# Revit family: P500236-030
name_source: partatom
category: Lighting Fixtures
revit_build: Autodesk Revit 2014 (Build: 20130308_1515(x64)
units: mm (PartAtom-declared; Revit-internal decimal feet)

## types (1)
- P500236-030
    Apparent Load = 75 VA
    Assembly Code = D5020200
    Color Filter = 16777215
    Connector Description = Lighting Connector
    Default Elevation = 48"
    Description = Select a light fixture that is gushing with rustic farmhouse charm with the Bastille Collection One-Light White Mini-Pendant. A country basket shade is coated in a black farmhouse-inspired finish. A metal covering coated in a crisp white finish contrasts with the black basket shade as it holds the light source in place.
    Diameter = 12"
    Dimming Lamp Color Temperature Shift = <None>
    Fixture distribution = Direct
    Glass = Hubbell - Glass
    Gold = Hubbell - Gold
    Height = 14 1/4"
    Housing Material = Paint - Hubbell - Metallic Bronze Textured
    Lamp = A-19
    Load Classification = Lighting
    Manufacturer = Progress Lighting
    Model = P500236-030
    Photometric Web File = generic
    Power Factor = 1
    Product Documentation Link = https://hubbellcdn.com
    Product Link = https://www.hubbell.com
    Specifications = Mini-pendant gushing with rustic farmhouse charm.
A country basket shade is coated in a black farmhouse-inspired finish.
A metal covering coated in a crisp white finish contrasts with the black basket shade.
Ideal for any foyer, kitchen, or dining room.
Perfect for rustic, farmhouse, or coastal settings.
Measures 12-inch width by 14-1/4-inch height.
Uses one medium base bulb that is sold separately (60w max - LED or incandescent).
Able to be fully dimmable with dimmable bulbs.
Includes installation instructions and mounting hardware.
Progress Lighting products are designed for exceptional quality, reliability, and functionality.
    Tilt Angle = 60.00°
    URL = https://www.hubbell.com
    Voltage = 120 V
    Warranty = 5 years Warranty
    Wattage Comments = 75W
    Watts = 75 W
    White = Paint - Hubbell - Matte White

## geometry (parser evidence)
native form markers: Sweep x6
no freeform markers — native parametric forms only
